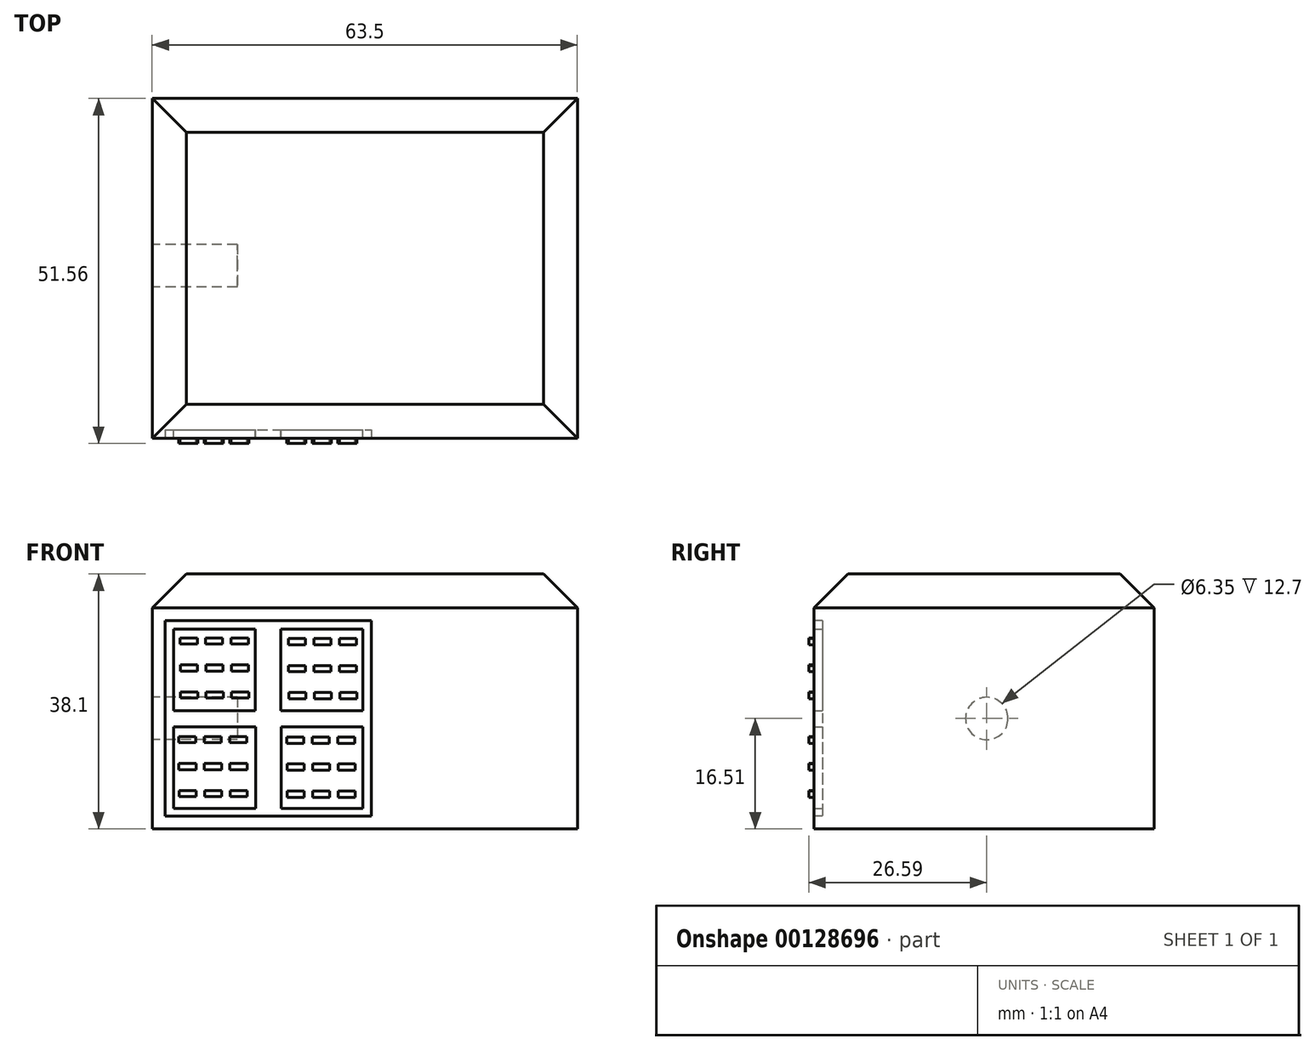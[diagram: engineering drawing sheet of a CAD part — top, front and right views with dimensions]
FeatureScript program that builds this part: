
annotation { "Feature Type Name" : "Feature", "Feature Type Description" : "" }
export const myFeature = defineFeature(function(context is Context, id is Id, definition is map)
    precondition{}
    {
        {
            var Q0;
            Q0=qCreatedBy(makeId("Top.planeOp"),FACE);
            var sketch = newSketch(context, id + "F0", { "sketchPlane" : qUnion([Q0])});
            skLineSegment(sketch, "E0.bottom", {"start": v(-33.94, 24.97) * mm, "end": v(29.56, 24.97) * mm});
            skLineSegment(sketch, "E0.top", {"start": v(-33.94, -25.83) * mm, "end": v(29.56, -25.83) * mm});
            skLineSegment(sketch, "E0.left", {"start": v(-33.94, 24.97) * mm, "end": v(-33.94, -25.83) * mm});
            skLineSegment(sketch, "E0.right", {"start": v(29.56, 24.97) * mm, "end": v(29.56, -25.83) * mm});
            skSolve(sketch);
        }
        {
            var Q0;
            Q0 = qSketchRegion(id + "F0", true);
            extrude(context, id + "F1", {"entities" : qUnion([Q0]), "depth" : 38.1 * mm});
        }
        {
            var Q0;
            Q0=makeQuery(id+"F1.opExtrude","CAP_EDGE",EDGE,{"disambiguationData":[OSD([sQuery(id+"F0.wireOp",EDGE,"E0.left")])],"isStart":false});
            var Q1;
            Q1=makeQuery(id+"F1.opExtrude","CAP_EDGE",EDGE,{"disambiguationData":[OSD([sQuery(id+"F0.wireOp",EDGE,"E0.top")])],"isStart":false});
            var Q2;
            Q2=makeQuery(id+"F1.opExtrude","CAP_EDGE",EDGE,{"disambiguationData":[OSD([sQuery(id+"F0.wireOp",EDGE,"E0.right")])],"isStart":false});
            var Q3;
            Q3=makeQuery(id+"F1.opExtrude","CAP_EDGE",EDGE,{"disambiguationData":[OSD([sQuery(id+"F0.wireOp",EDGE,"E0.bottom")])],"isStart":false});
            chamfer(context, id + "F2", {"entities" : qUnion([Q0, Q1, Q2, Q3]), "width" : 5.08 * mm, "tangentPropagation" : true});
        }
        {
            var Q0;
            Q0=makeQuery(id+"F1.opExtrude","SWEPT_FACE",FACE,{"disambiguationData":[OSD([sQuery(id+"F0.wireOp",EDGE,"E0.left")])]});
            var sketch = newSketch(context, id + "F3", { "sketchPlane" : qUnion([Q0])});
            skCircle(sketch, "E1", {"center": v(0, 16.51) * mm, "radius": 3.18 * mm});
            skPoint(sketch, "E1.centerSnap0", {"position": v(-24.97, 16.51) * mm});
            skSolve(sketch);
        }
        {
            var Q0;
            Q0 = qSketchRegion(id + "F3", true);
            extrude(context, id + "F4", {"entities" : qUnion([Q0]), "operationType" : NewBodyOperationType.REMOVE, "oppositeDirection" : true, "depth" : 12.7 * mm});
        }
        {
            var Q0;
            Q0=makeQuery(id+"F1.opExtrude","SWEPT_FACE",FACE,{"disambiguationData":[OSD([sQuery(id+"F0.wireOp",EDGE,"E0.top")])]});
            var sketch = newSketch(context, id + "F5", { "sketchPlane" : qUnion([Q0])});
            skLineSegment(sketch, "E2.bottom", {"start": v(-32.03, 31.12) * mm, "end": v(-1.22, 31.12) * mm});
            skLineSegment(sketch, "E2.top", {"start": v(-32.03, 1.9) * mm, "end": v(-1.22, 1.9) * mm});
            skLineSegment(sketch, "E2.left", {"start": v(-32.03, 31.12) * mm, "end": v(-32.03, 1.9) * mm});
            skLineSegment(sketch, "E2.right", {"start": v(-1.22, 31.12) * mm, "end": v(-1.22, 1.9) * mm});
            skLineSegment(sketch, "E3.0.0", {"start": v(29.56, 0) * mm, "end": v(29.56, 33.02) * mm});
            skLineSegment(sketch, "E3.0.1", {"start": v(29.56, 33.02) * mm, "end": v(-33.94, 33.02) * mm});
            skLineSegment(sketch, "E3.0.2", {"start": v(-33.94, 33.02) * mm, "end": v(-33.94, 0) * mm});
            skLineSegment(sketch, "E3.0.3", {"start": v(-33.94, 0) * mm, "end": v(29.56, 0) * mm});
            skSolve(sketch);
        }
        {
            var Q0;
            Q0=makeQuery(id+"F5.imprint","IMPRINT",FACE,{"disambiguationData":[TD([[makeQuery(id+"F5.imprint","IMPRINT",EDGE,{"derivedFrom":sQuery(id+"F5.wireOp",EDGE,"E2.bottom")}),-1.0]])]});
            extrude(context, id + "F6", {"entities" : qUnion([Q0]), "operationType" : NewBodyOperationType.REMOVE, "oppositeDirection" : true, "depth" : 1.27 * mm});
        }
        {
            var Q0;
            Q0=makeQuery(id+"F6.boolean.opBoolean","COPY",FACE,{"derivedFrom":makeQuery(id+"F6.opExtrude","CAP_FACE",FACE,{"disambiguationData":[OSD([sQuery(id+"F5.wireOp",EDGE,"E2.bottom"),sQuery(id+"F5.wireOp",EDGE,"E2.top"),sQuery(id+"F5.wireOp",EDGE,"E2.left"),sQuery(id+"F5.wireOp",EDGE,"E2.right")])],"isStart":false})});
            var sketch = newSketch(context, id + "F7", { "sketchPlane" : qUnion([Q0])});
            skLineSegment(sketch, "E4.bottom", {"start": v(-30.76, 29.84) * mm, "end": v(-18.56, 29.84) * mm});
            skLineSegment(sketch, "E4.top", {"start": v(-30.76, 17.65) * mm, "end": v(-18.56, 17.65) * mm});
            skLineSegment(sketch, "E4.left", {"start": v(-30.76, 29.84) * mm, "end": v(-30.76, 17.65) * mm});
            skLineSegment(sketch, "E4.right", {"start": v(-18.56, 29.84) * mm, "end": v(-18.56, 17.65) * mm});
            skLineSegment(sketch, "E5.1.0.0", {"start": v(-14.7, 29.84) * mm, "end": v(-2.5, 29.84) * mm});
            skLineSegment(sketch, "E5.1.0.1", {"start": v(-14.7, 29.84) * mm, "end": v(-14.7, 17.65) * mm});
            skLineSegment(sketch, "E5.1.0.2", {"start": v(-14.7, 17.65) * mm, "end": v(-2.5, 17.65) * mm});
            skLineSegment(sketch, "E5.1.0.3", {"start": v(-2.5, 29.84) * mm, "end": v(-2.5, 17.65) * mm});
            skLineSegment(sketch, "E6.1.0.0", {"start": v(-18.5, 15.28) * mm, "end": v(-18.5, 3.1) * mm});
            skLineSegment(sketch, "E6.1.0.1", {"start": v(-30.7, 15.28) * mm, "end": v(-30.7, 3.1) * mm});
            skLineSegment(sketch, "E6.1.0.2", {"start": v(-14.66, 15.28) * mm, "end": v(-2.45, 15.28) * mm});
            skLineSegment(sketch, "E6.1.0.3", {"start": v(-14.66, 15.28) * mm, "end": v(-14.66, 3.1) * mm});
            skLineSegment(sketch, "E6.1.0.4", {"start": v(-30.7, 3.1) * mm, "end": v(-18.5, 3.1) * mm});
            skLineSegment(sketch, "E6.1.0.5", {"start": v(-2.45, 15.28) * mm, "end": v(-2.45, 3.1) * mm});
            skLineSegment(sketch, "E6.1.0.6", {"start": v(-14.66, 3.1) * mm, "end": v(-2.45, 3.1) * mm});
            skLineSegment(sketch, "E6.1.0.7", {"start": v(-30.7, 15.28) * mm, "end": v(-18.5, 15.28) * mm});
            skLineSegment(sketch, "E6.direction1", {"start": v(-30.76, 17.65) * mm, "end": v(-30.7, 3.1) * mm, "construction": true});
            skSolve(sketch);
        }
        {
            var Q0;
            Q0 = qSketchRegion(id + "F7", true);
            extrude(context, id + "F8", {"entities" : qUnion([Q0]), "operationType" : NewBodyOperationType.ADD, "depth" : 1.27 * mm});
        }
        {
            var Q0;
            Q0=makeQuery(id+"F8.opExtrude","CAP_FACE",FACE,{"disambiguationData":[OSD([sQuery(id+"F7.wireOp",EDGE,"E4.bottom"),sQuery(id+"F7.wireOp",EDGE,"E4.top"),sQuery(id+"F7.wireOp",EDGE,"E4.left"),sQuery(id+"F7.wireOp",EDGE,"E4.right")])],"isStart":false});
            var sketch = newSketch(context, id + "F9", { "sketchPlane" : qUnion([Q0])});
            skLineSegment(sketch, "E7.0.0", {"start": v(-18.56, 29.84) * mm, "end": v(-30.76, 29.84) * mm});
            skLineSegment(sketch, "E7.0.1", {"start": v(-30.76, 29.84) * mm, "end": v(-30.76, 17.65) * mm});
            skLineSegment(sketch, "E7.0.2", {"start": v(-30.76, 17.65) * mm, "end": v(-18.56, 17.65) * mm});
            skLineSegment(sketch, "E7.0.3", {"start": v(-18.56, 17.65) * mm, "end": v(-18.56, 29.84) * mm});
            skLineSegment(sketch, "E8.0.0", {"start": v(-2.5, 29.84) * mm, "end": v(-14.7, 29.84) * mm});
            skLineSegment(sketch, "E8.0.1", {"start": v(-14.7, 29.84) * mm, "end": v(-14.7, 17.65) * mm});
            skLineSegment(sketch, "E8.0.2", {"start": v(-14.7, 17.65) * mm, "end": v(-2.5, 17.65) * mm});
            skLineSegment(sketch, "E8.0.3", {"start": v(-2.5, 17.65) * mm, "end": v(-2.5, 29.84) * mm});
            skLineSegment(sketch, "E9.0.0", {"start": v(-2.45, 15.28) * mm, "end": v(-14.66, 15.28) * mm});
            skLineSegment(sketch, "E9.0.1", {"start": v(-14.66, 15.28) * mm, "end": v(-14.66, 3.1) * mm});
            skLineSegment(sketch, "E9.0.2", {"start": v(-14.66, 3.1) * mm, "end": v(-2.45, 3.1) * mm});
            skLineSegment(sketch, "E9.0.3", {"start": v(-2.45, 3.1) * mm, "end": v(-2.45, 15.28) * mm});
            skLineSegment(sketch, "E10.0.0", {"start": v(-18.5, 3.1) * mm, "end": v(-18.5, 15.28) * mm});
            skLineSegment(sketch, "E10.0.1", {"start": v(-18.5, 15.28) * mm, "end": v(-30.7, 15.28) * mm});
            skLineSegment(sketch, "E10.0.2", {"start": v(-30.7, 15.28) * mm, "end": v(-30.7, 3.1) * mm});
            skLineSegment(sketch, "E10.0.3", {"start": v(-30.7, 3.1) * mm, "end": v(-18.5, 3.1) * mm});
            skLineSegment(sketch, "E11.bottom", {"start": v(-29.75, 28.55) * mm, "end": v(-27.2, 28.55) * mm});
            skLineSegment(sketch, "E11.top", {"start": v(-29.75, 27.62) * mm, "end": v(-27.2, 27.62) * mm});
            skLineSegment(sketch, "E11.left", {"start": v(-29.75, 28.55) * mm, "end": v(-29.75, 27.62) * mm});
            skLineSegment(sketch, "E11.right", {"start": v(-27.2, 28.55) * mm, "end": v(-27.2, 27.62) * mm});
            skLineSegment(sketch, "E12.1.0.0", {"start": v(-25.94, 28.55) * mm, "end": v(-23.4, 28.55) * mm});
            skLineSegment(sketch, "E12.1.0.1", {"start": v(-25.94, 28.55) * mm, "end": v(-25.94, 27.62) * mm});
            skLineSegment(sketch, "E12.1.0.2", {"start": v(-25.94, 27.62) * mm, "end": v(-23.4, 27.62) * mm});
            skLineSegment(sketch, "E12.1.0.3", {"start": v(-23.4, 28.55) * mm, "end": v(-23.4, 27.62) * mm});
            skLineSegment(sketch, "E12.2.0.0", {"start": v(-22.13, 28.55) * mm, "end": v(-19.59, 28.55) * mm});
            skLineSegment(sketch, "E12.2.0.1", {"start": v(-22.13, 28.55) * mm, "end": v(-22.13, 27.62) * mm});
            skLineSegment(sketch, "E12.2.0.2", {"start": v(-22.13, 27.62) * mm, "end": v(-19.59, 27.62) * mm});
            skLineSegment(sketch, "E12.2.0.3", {"start": v(-19.59, 28.55) * mm, "end": v(-19.59, 27.62) * mm});
            skLineSegment(sketch, "E13.1.0.0", {"start": v(-22.1, 23.59) * mm, "end": v(-19.56, 23.59) * mm});
            skLineSegment(sketch, "E13.1.0.2", {"start": v(-29.72, 23.59) * mm, "end": v(-27.18, 23.59) * mm});
            skLineSegment(sketch, "E13.1.0.3", {"start": v(-22.1, 24.52) * mm, "end": v(-19.56, 24.52) * mm});
            skLineSegment(sketch, "E13.1.0.4", {"start": v(-25.91, 23.59) * mm, "end": v(-23.37, 23.59) * mm});
            skLineSegment(sketch, "E13.1.0.5", {"start": v(-25.91, 24.52) * mm, "end": v(-23.37, 24.52) * mm});
            skLineSegment(sketch, "E13.1.0.6", {"start": v(-29.72, 24.52) * mm, "end": v(-27.18, 24.52) * mm});
            skLineSegment(sketch, "E13.1.0.7", {"start": v(-25.91, 24.52) * mm, "end": v(-25.91, 23.59) * mm});
            skLineSegment(sketch, "E13.1.0.8", {"start": v(-27.18, 24.52) * mm, "end": v(-27.18, 23.59) * mm});
            skLineSegment(sketch, "E13.1.0.9", {"start": v(-23.37, 24.52) * mm, "end": v(-23.37, 23.59) * mm});
            skLineSegment(sketch, "E13.1.0.10", {"start": v(-22.1, 24.52) * mm, "end": v(-22.1, 23.59) * mm});
            skLineSegment(sketch, "E13.1.0.11", {"start": v(-29.72, 24.52) * mm, "end": v(-29.72, 23.59) * mm});
            skLineSegment(sketch, "E13.1.0.12", {"start": v(-19.56, 24.52) * mm, "end": v(-19.56, 23.59) * mm});
            skLineSegment(sketch, "E13.2.0.0", {"start": v(-22.07, 19.56) * mm, "end": v(-19.52, 19.56) * mm});
            skLineSegment(sketch, "E13.2.0.2", {"start": v(-29.69, 19.56) * mm, "end": v(-27.14, 19.56) * mm});
            skLineSegment(sketch, "E13.2.0.3", {"start": v(-22.07, 20.49) * mm, "end": v(-19.52, 20.49) * mm});
            skLineSegment(sketch, "E13.2.0.4", {"start": v(-25.88, 19.56) * mm, "end": v(-23.33, 19.56) * mm});
            skLineSegment(sketch, "E13.2.0.5", {"start": v(-25.88, 20.49) * mm, "end": v(-23.33, 20.49) * mm});
            skLineSegment(sketch, "E13.2.0.6", {"start": v(-29.69, 20.49) * mm, "end": v(-27.14, 20.49) * mm});
            skLineSegment(sketch, "E13.2.0.7", {"start": v(-25.88, 20.49) * mm, "end": v(-25.88, 19.56) * mm});
            skLineSegment(sketch, "E13.2.0.8", {"start": v(-27.14, 20.49) * mm, "end": v(-27.14, 19.56) * mm});
            skLineSegment(sketch, "E13.2.0.9", {"start": v(-23.33, 20.49) * mm, "end": v(-23.33, 19.56) * mm});
            skLineSegment(sketch, "E13.2.0.10", {"start": v(-22.07, 20.49) * mm, "end": v(-22.07, 19.56) * mm});
            skLineSegment(sketch, "E13.2.0.11", {"start": v(-29.69, 20.49) * mm, "end": v(-29.69, 19.56) * mm});
            skLineSegment(sketch, "E13.2.0.12", {"start": v(-19.52, 20.49) * mm, "end": v(-19.52, 19.56) * mm});
            skLineSegment(sketch, "E14.1.0.0", {"start": v(-9.76, 24.43) * mm, "end": v(-7.21, 24.43) * mm});
            skLineSegment(sketch, "E14.1.0.1", {"start": v(-9.73, 19.47) * mm, "end": v(-7.18, 19.47) * mm});
            skLineSegment(sketch, "E14.1.0.2", {"start": v(-5.92, 20.4) * mm, "end": v(-3.37, 20.4) * mm});
            skLineSegment(sketch, "E14.1.0.3", {"start": v(-13.6, 28.46) * mm, "end": v(-11.06, 28.46) * mm});
            skLineSegment(sketch, "E14.1.0.4", {"start": v(-5.98, 27.53) * mm, "end": v(-3.44, 27.53) * mm});
            skLineSegment(sketch, "E14.1.0.5", {"start": v(-13.54, 19.47) * mm, "end": v(-11, 19.47) * mm});
            skLineSegment(sketch, "E14.1.0.6", {"start": v(-9.8, 28.46) * mm, "end": v(-7.25, 28.46) * mm});
            skLineSegment(sketch, "E14.1.0.7", {"start": v(-13.54, 20.4) * mm, "end": v(-11, 20.4) * mm});
            skLineSegment(sketch, "E14.1.0.8", {"start": v(-13.57, 23.5) * mm, "end": v(-11.02, 23.5) * mm});
            skLineSegment(sketch, "E14.1.0.9", {"start": v(-13.6, 27.53) * mm, "end": v(-11.06, 27.53) * mm});
            skLineSegment(sketch, "E14.1.0.10", {"start": v(-13.57, 24.43) * mm, "end": v(-11.02, 24.43) * mm});
            skLineSegment(sketch, "E14.1.0.11", {"start": v(-9.73, 20.4) * mm, "end": v(-7.18, 20.4) * mm});
            skLineSegment(sketch, "E14.1.0.12", {"start": v(-5.95, 23.5) * mm, "end": v(-3.4, 23.5) * mm});
            skLineSegment(sketch, "E14.1.0.13", {"start": v(-5.95, 24.43) * mm, "end": v(-3.4, 24.43) * mm});
            skLineSegment(sketch, "E14.1.0.14", {"start": v(-5.92, 19.47) * mm, "end": v(-3.37, 19.47) * mm});
            skLineSegment(sketch, "E14.1.0.15", {"start": v(-5.98, 28.46) * mm, "end": v(-3.44, 28.46) * mm});
            skLineSegment(sketch, "E14.1.0.16", {"start": v(-9.8, 27.53) * mm, "end": v(-7.25, 27.53) * mm});
            skLineSegment(sketch, "E14.1.0.17", {"start": v(-9.76, 23.5) * mm, "end": v(-7.21, 23.5) * mm});
            skLineSegment(sketch, "E14.1.0.18", {"start": v(-3.44, 28.46) * mm, "end": v(-3.44, 27.53) * mm});
            skLineSegment(sketch, "E14.1.0.19", {"start": v(-7.18, 20.4) * mm, "end": v(-7.18, 19.47) * mm});
            skLineSegment(sketch, "E14.1.0.20", {"start": v(-5.98, 28.46) * mm, "end": v(-5.98, 27.53) * mm});
            skLineSegment(sketch, "E14.1.0.21", {"start": v(-11.06, 28.46) * mm, "end": v(-11.06, 27.53) * mm});
            skLineSegment(sketch, "E14.1.0.22", {"start": v(-11.02, 24.43) * mm, "end": v(-11.02, 23.5) * mm});
            skLineSegment(sketch, "E14.1.0.23", {"start": v(-3.37, 20.4) * mm, "end": v(-3.37, 19.47) * mm});
            skLineSegment(sketch, "E14.1.0.24", {"start": v(-7.21, 24.43) * mm, "end": v(-7.21, 23.5) * mm});
            skLineSegment(sketch, "E14.1.0.25", {"start": v(-3.4, 24.43) * mm, "end": v(-3.4, 23.5) * mm});
            skLineSegment(sketch, "E14.1.0.26", {"start": v(-7.25, 28.46) * mm, "end": v(-7.25, 27.53) * mm});
            skLineSegment(sketch, "E14.1.0.27", {"start": v(-5.92, 20.4) * mm, "end": v(-5.92, 19.47) * mm});
            skLineSegment(sketch, "E14.1.0.28", {"start": v(-9.8, 28.46) * mm, "end": v(-9.8, 27.53) * mm});
            skLineSegment(sketch, "E14.1.0.29", {"start": v(-9.73, 20.4) * mm, "end": v(-9.73, 19.47) * mm});
            skLineSegment(sketch, "E14.1.0.30", {"start": v(-5.95, 24.43) * mm, "end": v(-5.95, 23.5) * mm});
            skLineSegment(sketch, "E14.1.0.31", {"start": v(-13.6, 28.46) * mm, "end": v(-13.6, 27.53) * mm});
            skLineSegment(sketch, "E14.1.0.32", {"start": v(-13.54, 20.4) * mm, "end": v(-13.54, 19.47) * mm});
            skLineSegment(sketch, "E14.1.0.33", {"start": v(-9.76, 24.43) * mm, "end": v(-9.76, 23.5) * mm});
            skLineSegment(sketch, "E14.1.0.34", {"start": v(-11, 20.4) * mm, "end": v(-11, 19.47) * mm});
            skLineSegment(sketch, "E14.1.0.35", {"start": v(-13.57, 24.43) * mm, "end": v(-13.57, 23.5) * mm});
            skLineSegment(sketch, "E15.1.0.0", {"start": v(-26.17, 13.83) * mm, "end": v(-23.62, 13.83) * mm});
            skLineSegment(sketch, "E15.1.0.1", {"start": v(-22.32, 8.87) * mm, "end": v(-19.78, 8.87) * mm});
            skLineSegment(sketch, "E15.1.0.2", {"start": v(-26.1, 5.77) * mm, "end": v(-23.56, 5.77) * mm});
            skLineSegment(sketch, "E15.1.0.3", {"start": v(-29.91, 5.77) * mm, "end": v(-27.37, 5.77) * mm});
            skLineSegment(sketch, "E15.1.0.4", {"start": v(-29.94, 8.87) * mm, "end": v(-27.4, 8.87) * mm});
            skLineSegment(sketch, "E15.1.0.5", {"start": v(-22.32, 9.8) * mm, "end": v(-19.78, 9.8) * mm});
            skLineSegment(sketch, "E15.1.0.6", {"start": v(-22.36, 12.9) * mm, "end": v(-19.81, 12.9) * mm});
            skLineSegment(sketch, "E15.1.0.7", {"start": v(-22.3, 5.77) * mm, "end": v(-19.75, 5.77) * mm});
            skLineSegment(sketch, "E15.1.0.8", {"start": v(-26.17, 12.9) * mm, "end": v(-23.62, 12.9) * mm});
            skLineSegment(sketch, "E15.1.0.9", {"start": v(-26.13, 8.87) * mm, "end": v(-23.59, 8.87) * mm});
            skLineSegment(sketch, "E15.1.0.10", {"start": v(-29.98, 13.83) * mm, "end": v(-27.43, 13.83) * mm});
            skLineSegment(sketch, "E15.1.0.11", {"start": v(-26.13, 9.8) * mm, "end": v(-23.59, 9.8) * mm});
            skLineSegment(sketch, "E15.1.0.12", {"start": v(-29.98, 12.9) * mm, "end": v(-27.43, 12.9) * mm});
            skLineSegment(sketch, "E15.1.0.13", {"start": v(-29.94, 9.8) * mm, "end": v(-27.4, 9.8) * mm});
            skLineSegment(sketch, "E15.1.0.14", {"start": v(-22.36, 13.83) * mm, "end": v(-19.81, 13.83) * mm});
            skLineSegment(sketch, "E15.1.0.16", {"start": v(-26.1, 4.84) * mm, "end": v(-23.56, 4.84) * mm});
            skLineSegment(sketch, "E15.1.0.17", {"start": v(-29.91, 4.84) * mm, "end": v(-27.37, 4.84) * mm});
            skLineSegment(sketch, "E15.1.0.18", {"start": v(-22.3, 4.84) * mm, "end": v(-19.75, 4.84) * mm});
            skLineSegment(sketch, "E15.1.0.19", {"start": v(-26.17, 13.83) * mm, "end": v(-26.17, 12.9) * mm});
            skLineSegment(sketch, "E15.1.0.20", {"start": v(-22.32, 9.8) * mm, "end": v(-22.32, 8.87) * mm});
            skLineSegment(sketch, "E15.1.0.21", {"start": v(-27.43, 13.83) * mm, "end": v(-27.43, 12.9) * mm});
            skLineSegment(sketch, "E15.1.0.22", {"start": v(-23.59, 9.8) * mm, "end": v(-23.59, 8.87) * mm});
            skLineSegment(sketch, "E15.1.0.23", {"start": v(-26.1, 5.77) * mm, "end": v(-26.1, 4.84) * mm});
            skLineSegment(sketch, "E15.1.0.24", {"start": v(-27.4, 9.8) * mm, "end": v(-27.4, 8.87) * mm});
            skLineSegment(sketch, "E15.1.0.25", {"start": v(-22.36, 13.83) * mm, "end": v(-22.36, 12.9) * mm});
            skLineSegment(sketch, "E15.1.0.26", {"start": v(-27.37, 5.77) * mm, "end": v(-27.37, 4.84) * mm});
            skLineSegment(sketch, "E15.1.0.27", {"start": v(-29.94, 9.8) * mm, "end": v(-29.94, 8.87) * mm});
            skLineSegment(sketch, "E15.1.0.28", {"start": v(-23.56, 5.77) * mm, "end": v(-23.56, 4.84) * mm});
            skLineSegment(sketch, "E15.1.0.29", {"start": v(-23.62, 13.83) * mm, "end": v(-23.62, 12.9) * mm});
            skLineSegment(sketch, "E15.1.0.30", {"start": v(-22.3, 5.77) * mm, "end": v(-22.3, 4.84) * mm});
            skLineSegment(sketch, "E15.1.0.31", {"start": v(-29.98, 13.83) * mm, "end": v(-29.98, 12.9) * mm});
            skLineSegment(sketch, "E15.1.0.32", {"start": v(-29.91, 5.77) * mm, "end": v(-29.91, 4.84) * mm});
            skLineSegment(sketch, "E15.1.0.33", {"start": v(-26.13, 9.8) * mm, "end": v(-26.13, 8.87) * mm});
            skLineSegment(sketch, "E15.1.0.34", {"start": v(-19.81, 13.83) * mm, "end": v(-19.81, 12.9) * mm});
            skLineSegment(sketch, "E15.1.0.35", {"start": v(-19.75, 5.77) * mm, "end": v(-19.75, 4.84) * mm});
            skLineSegment(sketch, "E15.1.0.36", {"start": v(-19.78, 9.8) * mm, "end": v(-19.78, 8.87) * mm});
            skLineSegment(sketch, "E15.1.0.37", {"start": v(-9.95, 4.75) * mm, "end": v(-7.4, 4.75) * mm});
            skLineSegment(sketch, "E15.1.0.38", {"start": v(-13.8, 9.71) * mm, "end": v(-11.25, 9.71) * mm});
            skLineSegment(sketch, "E15.1.0.39", {"start": v(-9.98, 8.78) * mm, "end": v(-7.44, 8.78) * mm});
            skLineSegment(sketch, "E15.1.0.40", {"start": v(-13.82, 12.81) * mm, "end": v(-11.28, 12.81) * mm});
            skLineSegment(sketch, "E15.1.0.41", {"start": v(-10.01, 12.81) * mm, "end": v(-7.47, 12.81) * mm});
            skLineSegment(sketch, "E15.1.0.42", {"start": v(-9.98, 9.71) * mm, "end": v(-7.44, 9.71) * mm});
            skLineSegment(sketch, "E15.1.0.43", {"start": v(-13.8, 8.78) * mm, "end": v(-11.25, 8.78) * mm});
            skLineSegment(sketch, "E15.1.0.44", {"start": v(-13.76, 5.68) * mm, "end": v(-11.21, 5.68) * mm});
            skLineSegment(sketch, "E15.1.0.45", {"start": v(-10.01, 13.74) * mm, "end": v(-7.47, 13.74) * mm});
            skLineSegment(sketch, "E15.1.0.46", {"start": v(-6.2, 13.74) * mm, "end": v(-3.66, 13.74) * mm});
            skLineSegment(sketch, "E15.1.0.47", {"start": v(-13.76, 4.75) * mm, "end": v(-11.21, 4.75) * mm});
            skLineSegment(sketch, "E15.1.0.48", {"start": v(-9.95, 5.68) * mm, "end": v(-7.4, 5.68) * mm});
            skLineSegment(sketch, "E15.1.0.49", {"start": v(-6.14, 5.68) * mm, "end": v(-3.6, 5.68) * mm});
            skLineSegment(sketch, "E15.1.0.50", {"start": v(-6.17, 8.78) * mm, "end": v(-3.63, 8.78) * mm});
            skLineSegment(sketch, "E15.1.0.51", {"start": v(-13.82, 13.74) * mm, "end": v(-11.28, 13.74) * mm});
            skLineSegment(sketch, "E15.1.0.52", {"start": v(-6.17, 9.71) * mm, "end": v(-3.63, 9.71) * mm});
            skLineSegment(sketch, "E15.1.0.53", {"start": v(-6.2, 12.81) * mm, "end": v(-3.66, 12.81) * mm});
            skLineSegment(sketch, "E15.1.0.54", {"start": v(-6.14, 4.75) * mm, "end": v(-3.6, 4.75) * mm});
            skLineSegment(sketch, "E15.1.0.55", {"start": v(-7.47, 13.74) * mm, "end": v(-7.47, 12.81) * mm});
            skLineSegment(sketch, "E15.1.0.56", {"start": v(-3.6, 5.68) * mm, "end": v(-3.6, 4.75) * mm});
            skLineSegment(sketch, "E15.1.0.57", {"start": v(-9.98, 9.71) * mm, "end": v(-9.98, 8.78) * mm});
            skLineSegment(sketch, "E15.1.0.58", {"start": v(-13.76, 5.68) * mm, "end": v(-13.76, 4.75) * mm});
            skLineSegment(sketch, "E15.1.0.59", {"start": v(-3.63, 9.71) * mm, "end": v(-3.63, 8.78) * mm});
            skLineSegment(sketch, "E15.1.0.60", {"start": v(-7.44, 9.71) * mm, "end": v(-7.44, 8.78) * mm});
            skLineSegment(sketch, "E15.1.0.61", {"start": v(-11.25, 9.71) * mm, "end": v(-11.25, 8.78) * mm});
            skLineSegment(sketch, "E15.1.0.62", {"start": v(-13.82, 13.74) * mm, "end": v(-13.82, 12.81) * mm});
            skLineSegment(sketch, "E15.1.0.63", {"start": v(-11.28, 13.74) * mm, "end": v(-11.28, 12.81) * mm});
            skLineSegment(sketch, "E15.1.0.64", {"start": v(-11.21, 5.68) * mm, "end": v(-11.21, 4.75) * mm});
            skLineSegment(sketch, "E15.1.0.65", {"start": v(-6.14, 5.68) * mm, "end": v(-6.14, 4.75) * mm});
            skLineSegment(sketch, "E15.1.0.66", {"start": v(-3.66, 13.74) * mm, "end": v(-3.66, 12.81) * mm});
            skLineSegment(sketch, "E15.1.0.67", {"start": v(-10.01, 13.74) * mm, "end": v(-10.01, 12.81) * mm});
            skLineSegment(sketch, "E15.1.0.68", {"start": v(-13.8, 9.71) * mm, "end": v(-13.8, 8.78) * mm});
            skLineSegment(sketch, "E15.1.0.69", {"start": v(-7.4, 5.68) * mm, "end": v(-7.4, 4.75) * mm});
            skLineSegment(sketch, "E15.1.0.70", {"start": v(-9.95, 5.68) * mm, "end": v(-9.95, 4.75) * mm});
            skLineSegment(sketch, "E15.1.0.71", {"start": v(-6.2, 13.74) * mm, "end": v(-6.2, 12.81) * mm});
            skLineSegment(sketch, "E15.1.0.72", {"start": v(-6.17, 9.71) * mm, "end": v(-6.17, 8.78) * mm});
            skSolve(sketch);
        }
        {
            var Q0;
            Q0=makeQuery(id+"F9.imprint","IMPRINT",FACE,{"disambiguationData":[TD([[makeQuery(id+"F9.imprint","IMPRINT",EDGE,{"derivedFrom":sQuery(id+"F9.wireOp",EDGE,"E11.bottom")}),-1.0]])]});
            var Q1;
            Q1=makeQuery(id+"F9.imprint","IMPRINT",FACE,{"disambiguationData":[TD([[makeQuery(id+"F9.imprint","IMPRINT",EDGE,{"derivedFrom":sQuery(id+"F9.wireOp",EDGE,"E12.1.0.0")}),-1.0]])]});
            var Q2;
            Q2=makeQuery(id+"F9.imprint","IMPRINT",FACE,{"disambiguationData":[TD([[makeQuery(id+"F9.imprint","IMPRINT",EDGE,{"derivedFrom":sQuery(id+"F9.wireOp",EDGE,"E12.2.0.0")}),-1.0]])]});
            var Q3;
            Q3=makeQuery(id+"F9.imprint","IMPRINT",FACE,{"disambiguationData":[TD([[makeQuery(id+"F9.imprint","IMPRINT",EDGE,{"derivedFrom":sQuery(id+"F9.wireOp",EDGE,"E13.1.0.2")}),1.0]])]});
            var Q4;
            Q4=makeQuery(id+"F9.imprint","IMPRINT",FACE,{"disambiguationData":[TD([[makeQuery(id+"F9.imprint","IMPRINT",EDGE,{"derivedFrom":sQuery(id+"F9.wireOp",EDGE,"E13.1.0.4")}),1.0]])]});
            var Q5;
            Q5=makeQuery(id+"F9.imprint","IMPRINT",FACE,{"disambiguationData":[TD([[makeQuery(id+"F9.imprint","IMPRINT",EDGE,{"derivedFrom":sQuery(id+"F9.wireOp",EDGE,"E13.1.0.0")}),1.0]])]});
            var Q6;
            Q6=makeQuery(id+"F9.imprint","IMPRINT",FACE,{"disambiguationData":[TD([[makeQuery(id+"F9.imprint","IMPRINT",EDGE,{"derivedFrom":sQuery(id+"F9.wireOp",EDGE,"E13.2.0.0")}),1.0]])]});
            var Q7;
            Q7=makeQuery(id+"F9.imprint","IMPRINT",FACE,{"disambiguationData":[TD([[makeQuery(id+"F9.imprint","IMPRINT",EDGE,{"derivedFrom":sQuery(id+"F9.wireOp",EDGE,"E13.2.0.4")}),1.0]])]});
            var Q8;
            Q8=makeQuery(id+"F9.imprint","IMPRINT",FACE,{"disambiguationData":[TD([[makeQuery(id+"F9.imprint","IMPRINT",EDGE,{"derivedFrom":sQuery(id+"F9.wireOp",EDGE,"E13.2.0.2")}),1.0]])]});
            var Q9;
            Q9=makeQuery(id+"F9.imprint","IMPRINT",FACE,{"disambiguationData":[TD([[makeQuery(id+"F9.imprint","IMPRINT",EDGE,{"derivedFrom":sQuery(id+"F9.wireOp",EDGE,"E15.1.0.10")}),-1.0]])]});
            var Q10;
            Q10=makeQuery(id+"F9.imprint","IMPRINT",FACE,{"disambiguationData":[TD([[makeQuery(id+"F9.imprint","IMPRINT",EDGE,{"derivedFrom":sQuery(id+"F9.wireOp",EDGE,"E15.1.0.0")}),-1.0]])]});
            var Q11;
            Q11=makeQuery(id+"F9.imprint","IMPRINT",FACE,{"disambiguationData":[TD([[makeQuery(id+"F9.imprint","IMPRINT",EDGE,{"derivedFrom":sQuery(id+"F9.wireOp",EDGE,"E15.1.0.6")}),1.0]])]});
            var Q12;
            Q12=makeQuery(id+"F9.imprint","IMPRINT",FACE,{"disambiguationData":[TD([[makeQuery(id+"F9.imprint","IMPRINT",EDGE,{"derivedFrom":sQuery(id+"F9.wireOp",EDGE,"E15.1.0.1")}),1.0]])]});
            var Q13;
            Q13=makeQuery(id+"F9.imprint","IMPRINT",FACE,{"disambiguationData":[TD([[makeQuery(id+"F9.imprint","IMPRINT",EDGE,{"derivedFrom":sQuery(id+"F9.wireOp",EDGE,"E15.1.0.9")}),1.0]])]});
            var Q14;
            Q14=makeQuery(id+"F9.imprint","IMPRINT",FACE,{"disambiguationData":[TD([[makeQuery(id+"F9.imprint","IMPRINT",EDGE,{"derivedFrom":sQuery(id+"F9.wireOp",EDGE,"E15.1.0.4")}),1.0]])]});
            var Q15;
            Q15=makeQuery(id+"F9.imprint","IMPRINT",FACE,{"disambiguationData":[TD([[makeQuery(id+"F9.imprint","IMPRINT",EDGE,{"derivedFrom":sQuery(id+"F9.wireOp",EDGE,"E15.1.0.3")}),-1.0]])]});
            var Q16;
            Q16=makeQuery(id+"F9.imprint","IMPRINT",FACE,{"disambiguationData":[TD([[makeQuery(id+"F9.imprint","IMPRINT",EDGE,{"derivedFrom":sQuery(id+"F9.wireOp",EDGE,"E15.1.0.2")}),-1.0]])]});
            var Q17;
            Q17=makeQuery(id+"F9.imprint","IMPRINT",FACE,{"disambiguationData":[TD([[makeQuery(id+"F9.imprint","IMPRINT",EDGE,{"derivedFrom":sQuery(id+"F9.wireOp",EDGE,"E15.1.0.7")}),-1.0]])]});
            var Q18;
            Q18=makeQuery(id+"F9.imprint","IMPRINT",FACE,{"disambiguationData":[TD([[makeQuery(id+"F9.imprint","IMPRINT",EDGE,{"derivedFrom":sQuery(id+"F9.wireOp",EDGE,"E15.1.0.38")}),-1.0]])]});
            var Q19;
            Q19=makeQuery(id+"F9.imprint","IMPRINT",FACE,{"disambiguationData":[TD([[makeQuery(id+"F9.imprint","IMPRINT",EDGE,{"derivedFrom":sQuery(id+"F9.wireOp",EDGE,"E15.1.0.40")}),1.0]])]});
            var Q20;
            Q20=makeQuery(id+"F9.imprint","IMPRINT",FACE,{"disambiguationData":[TD([[makeQuery(id+"F9.imprint","IMPRINT",EDGE,{"derivedFrom":sQuery(id+"F9.wireOp",EDGE,"E15.1.0.41")}),1.0]])]});
            var Q21;
            Q21=makeQuery(id+"F9.imprint","IMPRINT",FACE,{"disambiguationData":[TD([[makeQuery(id+"F9.imprint","IMPRINT",EDGE,{"derivedFrom":sQuery(id+"F9.wireOp",EDGE,"E15.1.0.39")}),1.0]])]});
            var Q22;
            Q22=makeQuery(id+"F9.imprint","IMPRINT",FACE,{"disambiguationData":[TD([[makeQuery(id+"F9.imprint","IMPRINT",EDGE,{"derivedFrom":sQuery(id+"F9.wireOp",EDGE,"E15.1.0.50")}),1.0]])]});
            var Q23;
            Q23=makeQuery(id+"F9.imprint","IMPRINT",FACE,{"disambiguationData":[TD([[makeQuery(id+"F9.imprint","IMPRINT",EDGE,{"derivedFrom":sQuery(id+"F9.wireOp",EDGE,"E15.1.0.46")}),-1.0]])]});
            var Q24;
            Q24=makeQuery(id+"F9.imprint","IMPRINT",FACE,{"disambiguationData":[TD([[makeQuery(id+"F9.imprint","IMPRINT",EDGE,{"derivedFrom":sQuery(id+"F9.wireOp",EDGE,"E15.1.0.49")}),-1.0]])]});
            var Q25;
            Q25=makeQuery(id+"F9.imprint","IMPRINT",FACE,{"disambiguationData":[TD([[makeQuery(id+"F9.imprint","IMPRINT",EDGE,{"derivedFrom":sQuery(id+"F9.wireOp",EDGE,"E15.1.0.37")}),1.0]])]});
            var Q26;
            Q26=makeQuery(id+"F9.imprint","IMPRINT",FACE,{"disambiguationData":[TD([[makeQuery(id+"F9.imprint","IMPRINT",EDGE,{"derivedFrom":sQuery(id+"F9.wireOp",EDGE,"E15.1.0.44")}),-1.0]])]});
            var Q27;
            Q27=makeQuery(id+"F9.imprint","IMPRINT",FACE,{"disambiguationData":[TD([[makeQuery(id+"F9.imprint","IMPRINT",EDGE,{"derivedFrom":sQuery(id+"F9.wireOp",EDGE,"E14.1.0.3")}),-1.0]])]});
            var Q28;
            Q28=makeQuery(id+"F9.imprint","IMPRINT",FACE,{"disambiguationData":[TD([[makeQuery(id+"F9.imprint","IMPRINT",EDGE,{"derivedFrom":sQuery(id+"F9.wireOp",EDGE,"E14.1.0.6")}),-1.0]])]});
            var Q29;
            Q29=makeQuery(id+"F9.imprint","IMPRINT",FACE,{"disambiguationData":[TD([[makeQuery(id+"F9.imprint","IMPRINT",EDGE,{"derivedFrom":sQuery(id+"F9.wireOp",EDGE,"E14.1.0.4")}),1.0]])]});
            var Q30;
            Q30=makeQuery(id+"F9.imprint","IMPRINT",FACE,{"disambiguationData":[TD([[makeQuery(id+"F9.imprint","IMPRINT",EDGE,{"derivedFrom":sQuery(id+"F9.wireOp",EDGE,"E14.1.0.12")}),1.0]])]});
            var Q31;
            Q31=makeQuery(id+"F9.imprint","IMPRINT",FACE,{"disambiguationData":[TD([[makeQuery(id+"F9.imprint","IMPRINT",EDGE,{"derivedFrom":sQuery(id+"F9.wireOp",EDGE,"E14.1.0.0")}),-1.0]])]});
            var Q32;
            Q32=makeQuery(id+"F9.imprint","IMPRINT",FACE,{"disambiguationData":[TD([[makeQuery(id+"F9.imprint","IMPRINT",EDGE,{"derivedFrom":sQuery(id+"F9.wireOp",EDGE,"E14.1.0.8")}),1.0]])]});
            var Q33;
            Q33=makeQuery(id+"F9.imprint","IMPRINT",FACE,{"disambiguationData":[TD([[makeQuery(id+"F9.imprint","IMPRINT",EDGE,{"derivedFrom":sQuery(id+"F9.wireOp",EDGE,"E14.1.0.5")}),1.0]])]});
            var Q34;
            Q34=makeQuery(id+"F9.imprint","IMPRINT",FACE,{"disambiguationData":[TD([[makeQuery(id+"F9.imprint","IMPRINT",EDGE,{"derivedFrom":sQuery(id+"F9.wireOp",EDGE,"E14.1.0.1")}),1.0]])]});
            var Q35;
            Q35=makeQuery(id+"F9.imprint","IMPRINT",FACE,{"disambiguationData":[TD([[makeQuery(id+"F9.imprint","IMPRINT",EDGE,{"derivedFrom":sQuery(id+"F9.wireOp",EDGE,"E14.1.0.2")}),-1.0]])]});
            extrude(context, id + "F10", {"entities" : qUnion([Q0, Q1, Q2, Q3, Q4, Q5, Q6, Q7, Q8, Q9, Q10, Q11, Q12, Q13, Q14, Q15, Q16, Q17, Q18, Q19, Q20, Q21, Q22, Q23, Q24, Q25, Q26, Q27, Q28, Q29, Q30, Q31, Q32, Q33, Q34, Q35]), "operationType" : NewBodyOperationType.ADD, "depth" : 0.76 * mm});
        }
    });
